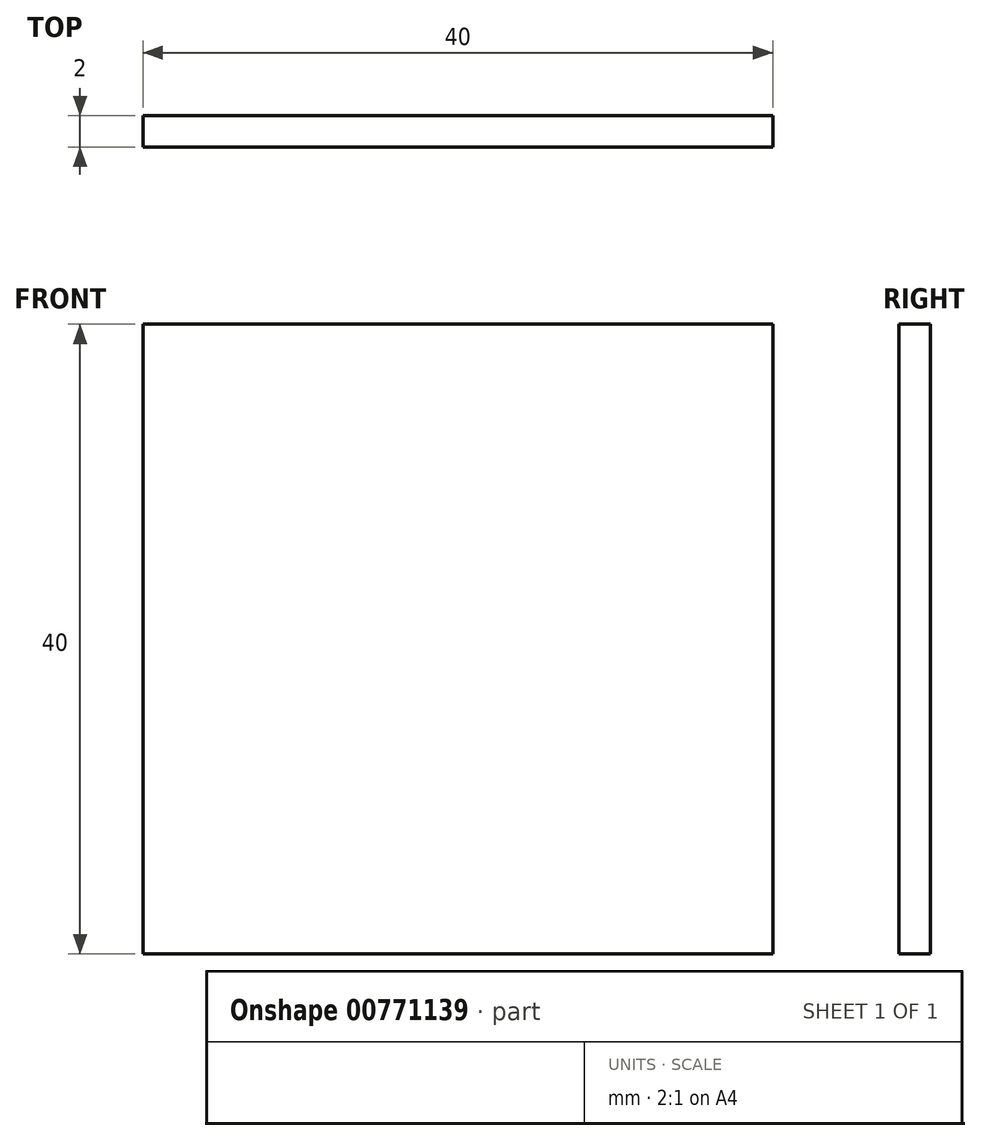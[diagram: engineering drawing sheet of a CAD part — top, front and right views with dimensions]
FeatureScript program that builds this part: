
annotation { "Feature Type Name" : "Feature", "Feature Type Description" : "" }
export const myFeature = defineFeature(function(context is Context, id is Id, definition is map)
    precondition{}
    {
        {
            var Q0;
            Q0=qCreatedBy(makeId("Front.planeOp"),FACE);
            var sketch = newSketch(context, id + "F0", { "sketchPlane" : qUnion([Q0])});
            skLineSegment(sketch, "E0.bottom", {"start": v(20, -20) * mm, "end": v(-20, -20) * mm});
            skLineSegment(sketch, "E0.top", {"start": v(20, 20) * mm, "end": v(-20, 20) * mm});
            skLineSegment(sketch, "E0.left", {"start": v(20, -20) * mm, "end": v(20, 20) * mm});
            skLineSegment(sketch, "E0.right", {"start": v(-20, -20) * mm, "end": v(-20, 20) * mm});
            skPoint(sketch, "E0.middle", {"position": v(0, 0) * mm});
            skSolve(sketch);
        }
        {
            var Q0;
            Q0 = qSketchRegion(id + "F0", true);
            extrude(context, id + "F1", {"entities" : qUnion([Q0]), "depth" : 2 * mm, "offsetDistance" : 25 * mm});
        }
    });
